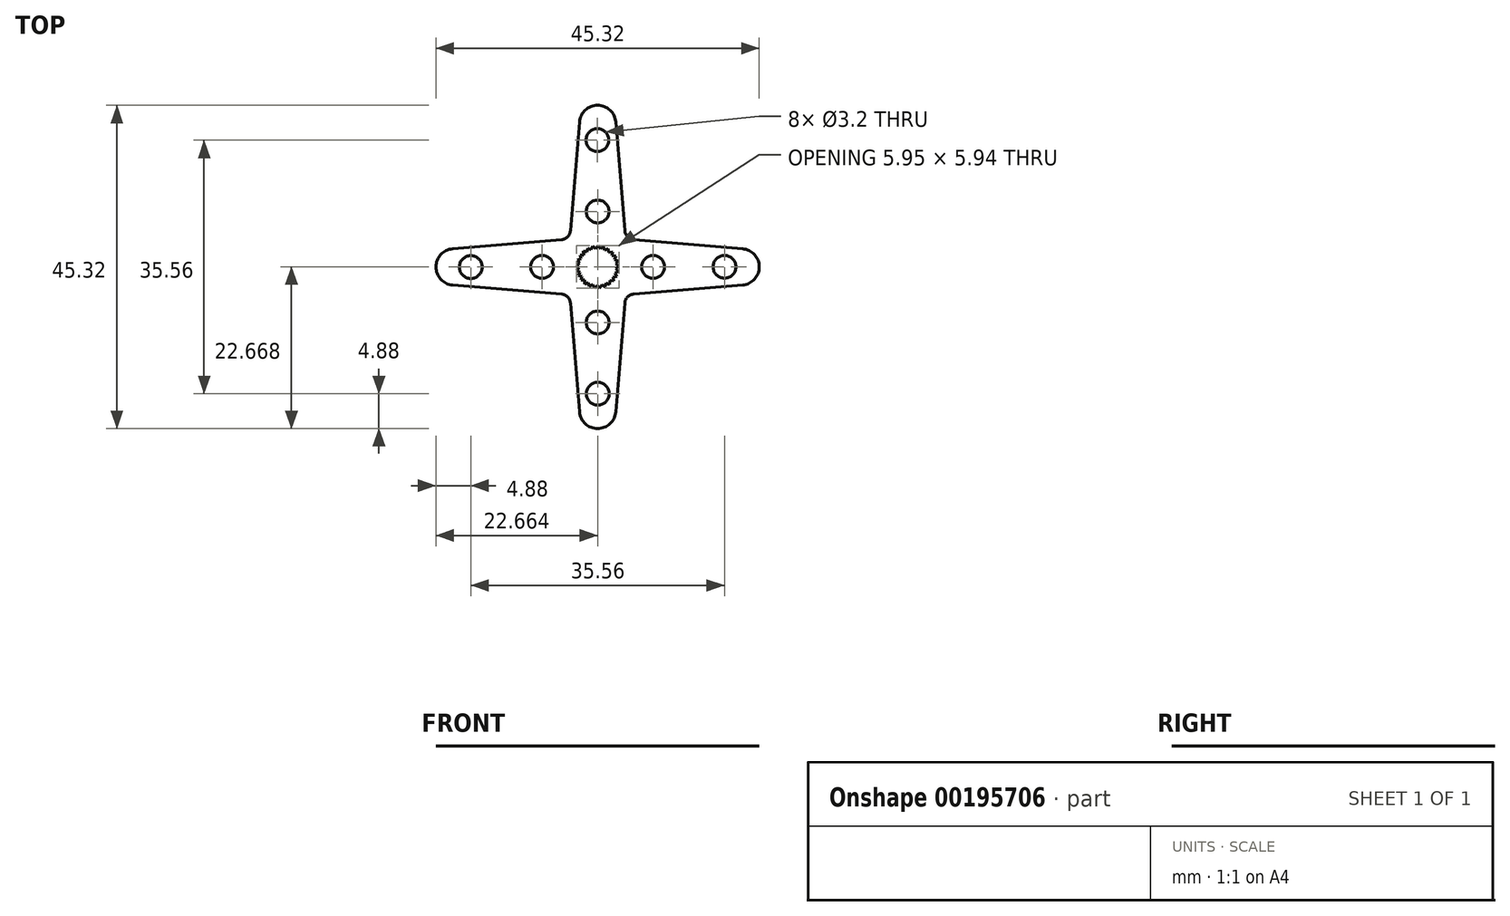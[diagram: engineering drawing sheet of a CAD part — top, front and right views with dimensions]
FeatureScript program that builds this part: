
annotation { "Feature Type Name" : "Feature", "Feature Type Description" : "" }
export const myFeature = defineFeature(function(context is Context, id is Id, definition is map)
    precondition{}
    {
        {
            var Q0;
            Q0=qCreatedBy(makeId("Top.planeOp"),FACE);
            var sketch = newSketch(context, id + "F0", { "sketchPlane" : qUnion([Q0])});
            skLineSegment(sketch, "E0", {"start": v(-2.48, 1.65) * mm, "end": v(-2.31, 1.15) * mm});
            skLineSegment(sketch, "E1", {"start": v(-2.31, 1.15) * mm, "end": v(-2.81, 0.98) * mm});
            skLineSegment(sketch, "E2.1.0", {"start": v(-2.81, 0.98) * mm, "end": v(-2.53, 0.54) * mm});
            skLineSegment(sketch, "E2.1.1", {"start": v(-2.53, 0.54) * mm, "end": v(-2.97, 0.25) * mm});
            skLineSegment(sketch, "E2.2.0", {"start": v(-2.97, 0.25) * mm, "end": v(-2.58, -0.1) * mm});
            skLineSegment(sketch, "E2.2.1", {"start": v(-2.58, -0.1) * mm, "end": v(-2.94, -0.5) * mm});
            skLineSegment(sketch, "E2.3.0", {"start": v(-2.94, -0.5) * mm, "end": v(-2.47, -0.74) * mm});
            skLineSegment(sketch, "E2.3.1", {"start": v(-2.47, -0.74) * mm, "end": v(-2.72, -1.2) * mm});
            skLineSegment(sketch, "E2.4.0", {"start": v(-2.72, -1.2) * mm, "end": v(-2.21, -1.34) * mm});
            skLineSegment(sketch, "E2.4.1", {"start": v(-2.21, -1.34) * mm, "end": v(-2.34, -1.85) * mm});
            skLineSegment(sketch, "E2.5.0", {"start": v(-2.34, -1.85) * mm, "end": v(-1.8, -1.84) * mm});
            skLineSegment(sketch, "E2.5.1", {"start": v(-1.8, -1.84) * mm, "end": v(-1.8, -2.37) * mm});
            skLineSegment(sketch, "E2.6.0", {"start": v(-1.8, -2.37) * mm, "end": v(-1.3, -2.24) * mm});
            skLineSegment(sketch, "E2.6.1", {"start": v(-1.3, -2.24) * mm, "end": v(-1.16, -2.75) * mm});
            skLineSegment(sketch, "E2.7.0", {"start": v(-1.16, -2.75) * mm, "end": v(-0.7, -2.49) * mm});
            skLineSegment(sketch, "E2.7.1", {"start": v(-0.7, -2.49) * mm, "end": v(-0.44, -2.95) * mm});
            skLineSegment(sketch, "E2.8.0", {"start": v(-0.44, -2.95) * mm, "end": v(-0.06, -2.58) * mm});
            skLineSegment(sketch, "E2.8.1", {"start": v(-0.06, -2.58) * mm, "end": v(0.3, -2.96) * mm});
            skLineSegment(sketch, "E2.9.0", {"start": v(0.3, -2.96) * mm, "end": v(0.59, -2.52) * mm});
            skLineSegment(sketch, "E2.9.1", {"start": v(0.59, -2.52) * mm, "end": v(1.04, -2.8) * mm});
            skLineSegment(sketch, "E2.10.0", {"start": v(1.04, -2.8) * mm, "end": v(1.2, -2.3) * mm});
            skLineSegment(sketch, "E2.10.1", {"start": v(1.2, -2.3) * mm, "end": v(1.7, -2.45) * mm});
            skLineSegment(sketch, "E2.11.0", {"start": v(1.7, -2.45) * mm, "end": v(1.73, -1.92) * mm});
            skLineSegment(sketch, "E2.11.1", {"start": v(1.73, -1.92) * mm, "end": v(2.25, -1.95) * mm});
            skLineSegment(sketch, "E2.12.0", {"start": v(2.25, -1.95) * mm, "end": v(2.15, -1.43) * mm});
            skLineSegment(sketch, "E2.12.1", {"start": v(2.15, -1.43) * mm, "end": v(2.67, -1.33) * mm});
            skLineSegment(sketch, "E2.13.0", {"start": v(2.67, -1.33) * mm, "end": v(2.44, -0.85) * mm});
            skLineSegment(sketch, "E2.13.1", {"start": v(2.44, -0.85) * mm, "end": v(2.91, -0.62) * mm});
            skLineSegment(sketch, "E2.14.0", {"start": v(2.91, -0.62) * mm, "end": v(2.57, -0.22) * mm});
            skLineSegment(sketch, "E2.14.1", {"start": v(2.57, -0.22) * mm, "end": v(2.98, 0.12) * mm});
            skLineSegment(sketch, "E2.15.0", {"start": v(2.98, 0.12) * mm, "end": v(2.55, 0.43) * mm});
            skLineSegment(sketch, "E2.15.1", {"start": v(2.55, 0.43) * mm, "end": v(2.85, 0.86) * mm});
            skLineSegment(sketch, "E2.16.0", {"start": v(2.85, 0.86) * mm, "end": v(2.36, 1.05) * mm});
            skLineSegment(sketch, "E2.16.1", {"start": v(2.36, 1.05) * mm, "end": v(2.55, 1.54) * mm});
            skLineSegment(sketch, "E2.17.0", {"start": v(2.55, 1.54) * mm, "end": v(2.03, 1.6) * mm});
            skLineSegment(sketch, "E2.17.1", {"start": v(2.03, 1.6) * mm, "end": v(2.09, 2.13) * mm});
            skLineSegment(sketch, "E2.18.0", {"start": v(2.09, 2.13) * mm, "end": v(1.56, 2.06) * mm});
            skLineSegment(sketch, "E2.18.1", {"start": v(1.56, 2.06) * mm, "end": v(1.5, 2.58) * mm});
            skLineSegment(sketch, "E2.19.0", {"start": v(1.5, 2.58) * mm, "end": v(1, 2.38) * mm});
            skLineSegment(sketch, "E2.19.1", {"start": v(1, 2.38) * mm, "end": v(0.8, 2.87) * mm});
            skLineSegment(sketch, "E2.20.0", {"start": v(0.8, 2.87) * mm, "end": v(0.38, 2.56) * mm});
            skLineSegment(sketch, "E2.20.1", {"start": v(0.38, 2.56) * mm, "end": v(0.07, 2.98) * mm});
            skLineSegment(sketch, "E2.21.0", {"start": v(0.07, 2.98) * mm, "end": v(-0.27, 2.57) * mm});
            skLineSegment(sketch, "E2.21.1", {"start": v(-0.27, 2.57) * mm, "end": v(-0.68, 2.9) * mm});
            skLineSegment(sketch, "E2.22.0", {"start": v(-0.68, 2.9) * mm, "end": v(-0.9, 2.42) * mm});
            skLineSegment(sketch, "E2.22.1", {"start": v(-0.9, 2.42) * mm, "end": v(-1.38, 2.64) * mm});
            skLineSegment(sketch, "E2.23.0", {"start": v(-1.38, 2.64) * mm, "end": v(-1.47, 2.12) * mm});
            skLineSegment(sketch, "E2.23.1", {"start": v(-1.47, 2.12) * mm, "end": v(-2, 2.22) * mm});
            skLineSegment(sketch, "E2.24.0", {"start": v(-2, 2.22) * mm, "end": v(-1.95, 1.69) * mm});
            skLineSegment(sketch, "E2.24.1", {"start": v(-1.95, 1.69) * mm, "end": v(-2.48, 1.65) * mm});
            skPoint(sketch, "E2.center", {"position": v(0, 0) * mm});
            skLineSegment(sketch, "E3", {"start": v(-5.08, 3.81) * mm, "end": v(-20.32, 2.54) * mm});
            skLineSegment(sketch, "E4", {"start": v(-5.08, -3.8) * mm, "end": v(-20.32, -2.54) * mm});
            skPoint(sketch, "E5", {"position": v(-2.7, 0) * mm});
            skCircle(sketch, "E6", {"center": v(-17.78, -0.02) * mm, "radius": 1.6 * mm});
            skArc(sketch, "E7", {"start": v(-20.32, 2.54) * mm, "mid": v(-22.66, 0) * mm, "end": v(-20.32, -2.54) * mm});
            skCircle(sketch, "E8", {"center": v(-7.78, 0) * mm, "radius": 1.6 * mm});
            skLineSegment(sketch, "E9.1.0", {"start": v(-3.81, -5.08) * mm, "end": v(-2.54, -20.32) * mm});
            skArc(sketch, "E9.1.1", {"start": v(-2.54, -20.32) * mm, "mid": v(0, -22.66) * mm, "end": v(2.54, -20.32) * mm});
            skLineSegment(sketch, "E9.1.2", {"start": v(3.8, -5.08) * mm, "end": v(2.54, -20.32) * mm});
            skCircle(sketch, "E9.1.3", {"center": v(0.02, -17.78) * mm, "radius": 1.6 * mm});
            skCircle(sketch, "E9.1.4", {"center": v(0, -7.78) * mm, "radius": 1.6 * mm});
            skLineSegment(sketch, "E9.2.0", {"start": v(5.08, -3.81) * mm, "end": v(20.32, -2.54) * mm});
            skArc(sketch, "E9.2.1", {"start": v(20.32, -2.54) * mm, "mid": v(22.66, 0) * mm, "end": v(20.32, 2.54) * mm});
            skLineSegment(sketch, "E9.2.2", {"start": v(5.08, 3.8) * mm, "end": v(20.32, 2.54) * mm});
            skCircle(sketch, "E9.2.3", {"center": v(17.78, 0.02) * mm, "radius": 1.6 * mm});
            skCircle(sketch, "E9.2.4", {"center": v(7.78, 0) * mm, "radius": 1.6 * mm});
            skLineSegment(sketch, "E9.3.0", {"start": v(3.81, 5.08) * mm, "end": v(2.54, 20.32) * mm});
            skArc(sketch, "E9.3.1", {"start": v(2.54, 20.32) * mm, "mid": v(0, 22.66) * mm, "end": v(-2.54, 20.32) * mm});
            skLineSegment(sketch, "E9.3.2", {"start": v(-3.8, 5.08) * mm, "end": v(-2.54, 20.32) * mm});
            skCircle(sketch, "E9.3.3", {"center": v(-0.02, 17.78) * mm, "radius": 1.6 * mm});
            skCircle(sketch, "E9.3.4", {"center": v(0, 7.78) * mm, "radius": 1.6 * mm});
            skArc(sketch, "E10", {"start": v(-5.08, 3.81) * mm, "mid": v(-4.2, 4.21) * mm, "end": v(-3.8, 5.08) * mm});
            skArc(sketch, "E11", {"start": v(3.8, 5.08) * mm, "mid": v(4.21, 4.21) * mm, "end": v(5.08, 3.8) * mm});
            skArc(sketch, "E12", {"start": v(5.08, -3.8) * mm, "mid": v(4.21, -4.21) * mm, "end": v(3.8, -5.08) * mm});
            skArc(sketch, "E13", {"start": v(-3.81, -5.08) * mm, "mid": v(-4.21, -4.21) * mm, "end": v(-5.08, -3.8) * mm});
            skSolve(sketch);
        }
        {
            var Q0;
            Q0=makeQuery(id+"F0.imprint","IMPRINT",FACE,{"disambiguationData":[TD([[makeQuery(id+"F0.imprint","IMPRINT",EDGE,{"derivedFrom":sQuery(id+"F0.wireOp",EDGE,"E0")}),-1.0]])]});
            extrude(context, id + "F1", {"entities" : qUnion([Q0]), "depth" : 1 / 203.2 * mm});
        }
    });
